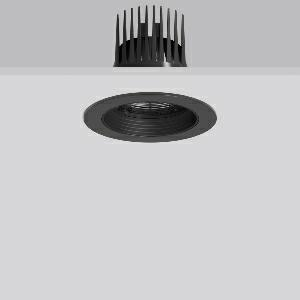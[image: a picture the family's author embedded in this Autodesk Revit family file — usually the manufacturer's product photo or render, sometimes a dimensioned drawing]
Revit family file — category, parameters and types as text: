
# Revit family: heledon_maxi_e_901782_003_c31d
name_source: partatom
category: Lighting Fixtures
units: mm (PartAtom-declared; Revit-internal decimal feet)

## family parameters
Cut with Voids When Loaded = No
Host = Face
Light Source = No
Part Type = Normal
Room Calculation Point = No
Round Connector Dimension = Use Diameter
Shared = No

## types (1)
- HELEDON maxi E (1 x LED Modul 920 meat+, 1850 lm, 2000)
    Apparent Load = 33 VA
    Approval mark = CE
    CIE Flux Codes = 96 99 100 100 100
    Color Rendering = 90
    Color Temperature = 2000
    Default Elevation = 1800 mm
    Description = Series: HELEDON maxi
Round recessed downlight. Housing: die-cast aluminium, powder-coated. Black plastic ring and recessed LED to prevent glare from the side. Optical assembly with lens made of plastic (polycarbonate) for the best homogeneous light distribution - can be changed without tools. Special LED for illumination of meat included. Suitable for Recessed ceiling mounting. Installation without tools thanks to spring fastening system. Including separate LED converter with connecting cable 600 mm.High quality converter without flickering and stroboscopic effect. Through-wiring box (5 pole) available as accessory. The following accessories can be mounted without use of tools: interchangeable lenses, decorative glasses, honeycomb louvre, clear and frosted diffusers, white interchangeable plastic ring. 
Colour: deep black, matt (RAL 9005)
Diameter: 162 mm
Height: 3 mm
Cut-out diameter: 152 mm
Recess height: 200 mm
Luminaire: recess height: 135 mm
Lamp: LED
Socket: without socket
Colour temperature: meat +
System power: 33 W
Rated luminous flux: 1850 lm
Luminous efficiency: 56 lm/W
Control gear: Regulated power supply
Protection class: II
Type of protection: IP 20
    Height = 0 mm  [stored 0 ft]
    Lamp = 1 x LED Modul 920 meat+
    Lamp Light Flux = 1850 lm
    Lamp count = 1
    Length = 162 mm
    Lifetime = 50000 h
    Luminous efficacy = 56 lm/W
    Manufacturer = RZB
    ModVariant = No
    Model = 901782.003
    Mounting Place = Ceiling
    Mounting Type = Recessed
    Number of Poles = 1
    OnlyDefault = Yes
    Power Factor = 1
    Product Name = HELEDON maxi E
    Product group = Recessed downlights
    ProductGroupID = 402
    Protection Class = Protection class II
    Protection Degree = IP 20
    RLX_Detail_Level = 1
    RLX_Emergency_Light_Flux = 0 lm
    RLX_Emergency_Type = 0
    RLX_Emergency_Type_DB = No
    RlxData = <blob elided: 121293 chars, md5=443f8e42>
    Socket = socket
    Standby Power = 0 W
    System Light Flux = 1850 lm
    System Power = 33 W
    Type Comments = Product without accessories
    Type Image = 901663.003.jpg
    URL = http://relux.com
    VarID = ---
    Voltage = 230 V
    Voltage Range = 220-240 V
    Weight = 0.00 kg
    Width = 0 mm  [stored 0 ft]

note: [stored X ft] marks values corroborated as IEEE doubles in the binary element streams (Revit-internal decimal feet)

## geometry (parser evidence)
native form markers: Blend x4, Sweep x12
no freeform markers — native parametric forms only
